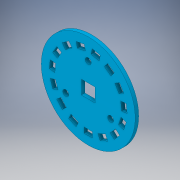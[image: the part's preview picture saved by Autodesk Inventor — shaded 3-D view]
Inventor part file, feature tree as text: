
AUTODESK INVENTOR PART (.ipt)
format: ipt  version: 2019.3 (Build 233278000, 278)  size: 216,576 bytes
history: native  units: in
note: dims shown in document units (in); Inventor stores cm internally (conversion verified against a paired STEP export)
features: sketch x4, extrude x3, hole x1
ambient origin geometry x8: Origin, YZ Plane, XZ Plane, XY Plane, X Axis, Y Axis, Z Axis, Center Point
bodies: Solid1 (feature_tree)
feature tree (8):
  extrude  "Extrusion1"  Depth=0.1in TaperAngle=0.0deg
  extrude  "Extrusion2"  Depth=0.3937in TaperAngle=0.0deg
  extrude  "Extrusion3"  Depth=0.1575in
  hole  "Hole1"  [1 undecoded]
  sketch  "Sketch1"  dims[d0=2.6772in d1=0.1in d2=0.0in]
  sketch  "Sketch2"  dims[d3=0.3937in d4=0.66in d5=0.0in]
  sketch  "Sketch3"  dims[d6=2.0472in d7=0.1575in]
  sketch  "Sketch4"  dims[d8=0.2362in d9=5.9055in d11=360.0deg d13=0.0in d14=0.0in d15=1.4765in d16=0.7383in d17=90.0deg d18=1.1811in d20=360.0deg d22=0.17in d23=0.75in d24=0.332in d25=0.25in d26=0.5635in d27=1.0in d28=0.8108in]
note: 1 required parameter value undecoded (feature->parameter linkage not recoverable at this tier; creation-order binding heuristic only, values carry confidence <= 0.55)
